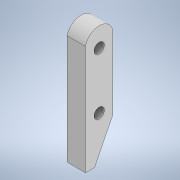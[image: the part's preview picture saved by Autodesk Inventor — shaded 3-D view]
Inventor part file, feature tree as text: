
AUTODESK INVENTOR PART (.ipt)
format: ipt  version: 2020 (Build 240168000, 168)  size: 124,416 bytes
history: native  units: in
note: dims shown in document units (in); Inventor stores cm internally (conversion verified against a paired STEP export)
features: extrude x4, sketch x4
ambient origin geometry x8: Origin, YZ Plane, XZ Plane, XY Plane, X Axis, Y Axis, Z Axis, Center Point
bodies: Solid1 (feature_tree)
feature tree (8):
  extrude  "Extrusion1"  Depth=0.375in
  extrude  "Extrusion2"  Depth=0.25in
  extrude  "Extrusion3"  Depth=0.141in
  extrude  "Extrusion4"  Depth=0.25in TaperAngle=0.0deg
  sketch  "Sketch1"  dims[d0=1.0in d1=0.375in]
  sketch  "Sketch2"  dims[d2=0.25in d3=0.0in d4=0.77in]
  sketch  "Sketch3"  dims[d5=0.141in d6=0.141in]
  sketch  "Sketch4"  dims[d7=0.5625in d8=0.0in d9=0.25in d10=0.0in d11=0.5in d12=0.125in d13=0.25in d14=0.0in]
